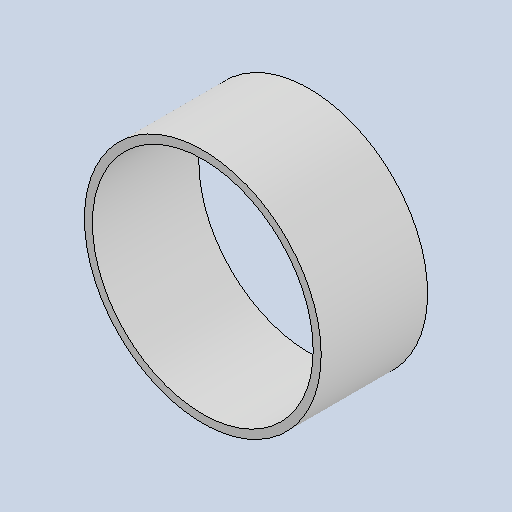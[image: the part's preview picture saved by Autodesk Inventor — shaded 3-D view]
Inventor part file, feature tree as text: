
AUTODESK INVENTOR PART (.ipt)
format: ipt  version: 2025 (Build 290162010, 162A)  size: 105,472 bytes
history: native  units: mm
features: extrude x1, sketch x1
ambient origin geometry x8: Origin, YZ Plane, XZ Plane, XY Plane, X Axis, Y Axis, Z Axis, Center Point
bodies: Solid1 (feature_tree)
feature tree (2):
  extrude  "Extrusion1"  Depth=40.0mm
  sketch  "Sketch1"  dims[d0=89.0mm d1=3.0mm d2=40.0mm d3=0.0mm]
